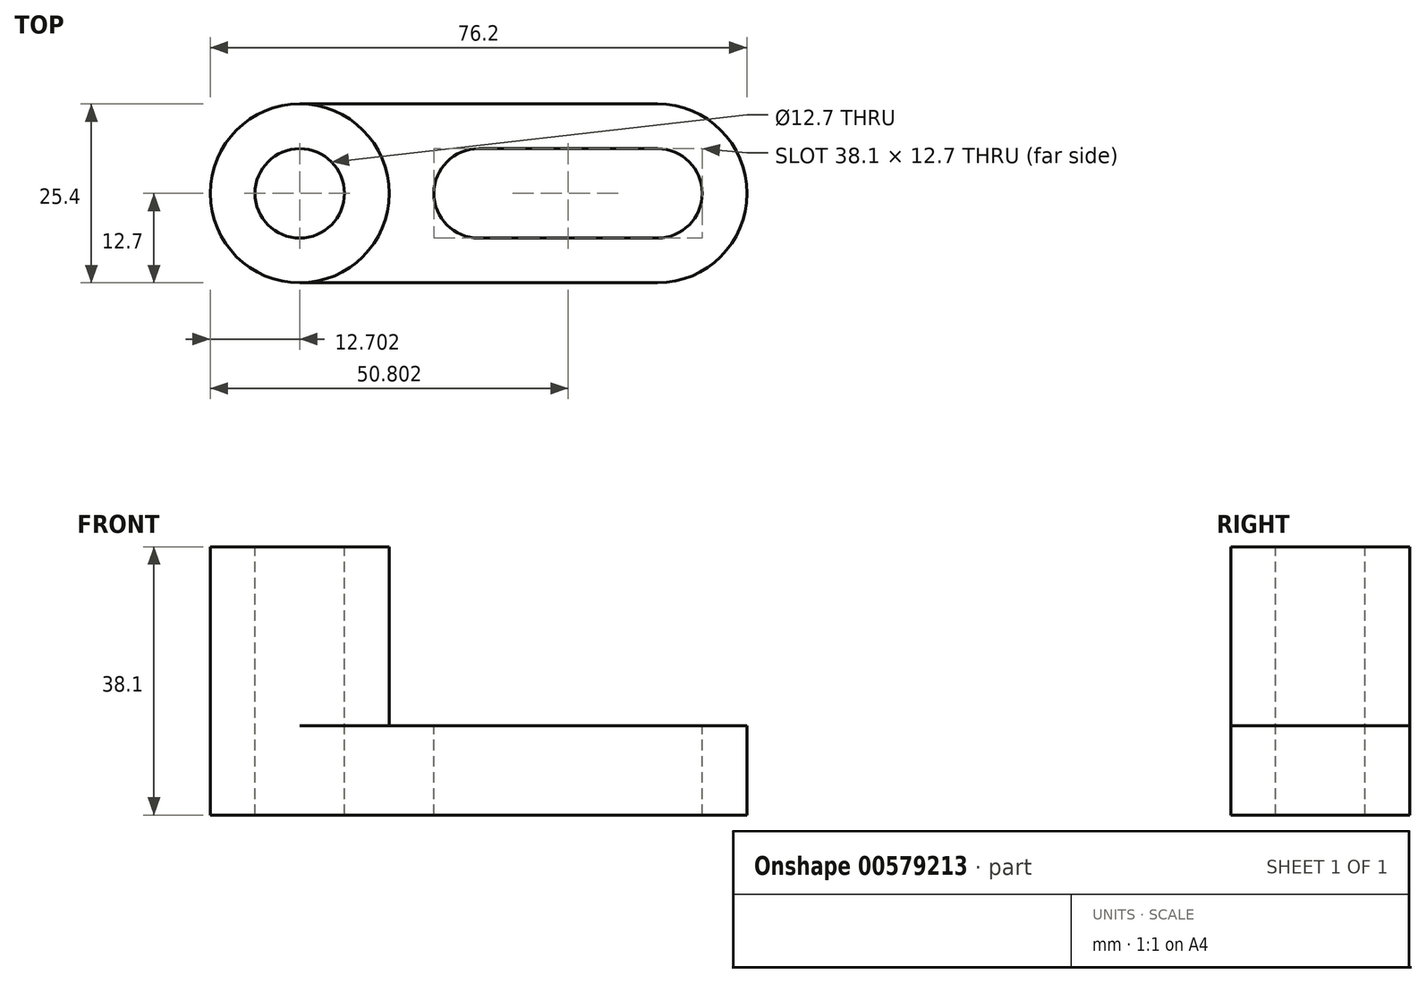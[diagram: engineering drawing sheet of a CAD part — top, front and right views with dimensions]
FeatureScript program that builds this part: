
annotation { "Feature Type Name" : "Feature", "Feature Type Description" : "" }
export const myFeature = defineFeature(function(context is Context, id is Id, definition is map)
    precondition{}
    {
        {
            var Q0;
            Q0=qCreatedBy(makeId("Front.planeOp"),FACE);
            var sketch = newSketch(context, id + "F0", { "sketchPlane" : qUnion([Q0])});
            skLineSegment(sketch, "E0", {"start": v(-84.2, 67.03) * mm, "end": v(-84.2, 28.93) * mm});
            skLineSegment(sketch, "E1", {"start": v(-84.2, 28.93) * mm, "end": v(-8, 28.93) * mm});
            skLineSegment(sketch, "E2", {"start": v(-8, 28.93) * mm, "end": v(-8, 41.63) * mm});
            skLineSegment(sketch, "E3", {"start": v(-8, 41.63) * mm, "end": v(-58.8, 41.63) * mm});
            skLineSegment(sketch, "E4", {"start": v(-58.8, 41.63) * mm, "end": v(-58.8, 67.03) * mm});
            skLineSegment(sketch, "E5", {"start": v(-58.8, 67.03) * mm, "end": v(-84.2, 67.03) * mm});
            skSolve(sketch);
        }
        {
            var Q0;
            Q0=makeQuery(id+"F0.imprint","IMPRINT",FACE,{"disambiguationData":[TD([[makeQuery(id+"F0.imprint","IMPRINT",EDGE,{"derivedFrom":sQuery(id+"F0.wireOp",EDGE,"E0")}),1.0]])]});
            extrude(context, id + "F1", {"entities" : qUnion([Q0]), "depth" : 25.4 * mm, "offsetDistance" : 25.4 * mm});
        }
        {
            var Q0;
            Q0=makeQuery(id+"F1.opExtrude","SWEPT_FACE",FACE,{"disambiguationData":[OSD([sQuery(id+"F0.wireOp",EDGE,"E3")])]});
            var sketch = newSketch(context, id + "F2", { "sketchPlane" : qUnion([Q0])});
            skCircle(sketch, "E6", {"center": v(-46.1, -12.7) * mm, "radius": 6.35 * mm});
            skCircle(sketch, "E7", {"center": v(-20.7, -12.7) * mm, "radius": 6.35 * mm});
            skLineSegment(sketch, "E8", {"start": v(-46.1, -6.35) * mm, "end": v(-20.7, -6.35) * mm});
            skLineSegment(sketch, "E9", {"start": v(-46.1, -19.05) * mm, "end": v(-20.7, -19.05) * mm});
            skSolve(sketch);
        }
        {
            var Q0;
            {var subQ0=sQuery(id+"F2.wireOp",EDGE,"E6");var subQ1=makeQuery(id+"F2.imprint","INTERSECT",VERTEX,{"derivedFrom":[subQ0,sQuery(id+"F2.wireOp",EDGE,"E8")]});Q0=makeQuery(id+"F2.imprint","IMPRINT",FACE,{"disambiguationData":[TD([[makeQuery(id+"F2.imprint","IMPRINT",EDGE,{"disambiguationData":[TD([[subQ1,-1.0]])],"derivedFrom":subQ0}),1.0]])]});}
            var Q1;
            {var subQ0=sQuery(id+"F2.wireOp",EDGE,"E8");Q1=makeQuery(id+"F2.imprint","IMPRINT",FACE,{"disambiguationData":[TD([[makeQuery(id+"F2.imprint","IMPRINT",EDGE,{"derivedFrom":subQ0}),-1.0]])]});}
            var Q2;
            {var subQ0=sQuery(id+"F2.wireOp",EDGE,"E7");var subQ1=makeQuery(id+"F2.imprint","INTERSECT",VERTEX,{"derivedFrom":[subQ0,sQuery(id+"F2.wireOp",EDGE,"E8")]});Q2=makeQuery(id+"F2.imprint","IMPRINT",FACE,{"disambiguationData":[TD([[makeQuery(id+"F2.imprint","IMPRINT",EDGE,{"disambiguationData":[TD([[subQ1,-1.0]])],"derivedFrom":subQ0}),1.0]])]});}
            extrude(context, id + "F3", {"entities" : qUnion([Q0, Q1, Q2]), "operationType" : NewBodyOperationType.REMOVE, "endBound" : BoundingType.THROUGH_ALL, "oppositeDirection" : true, "depth" : 25.4 * mm, "offsetDistance" : 25.4 * mm});
        }
        {
            var Q0;
            Q0=makeQuery(id+"F1.opExtrude","SWEPT_FACE",FACE,{"disambiguationData":[OSD([sQuery(id+"F0.wireOp",EDGE,"E5")])]});
            var sketch = newSketch(context, id + "F4", { "sketchPlane" : qUnion([Q0])});
            skCircle(sketch, "E10", {"center": v(-71.5, -12.7) * mm, "radius": 12.7 * mm});
            skSolve(sketch);
        }
        {
            var Q0;
            {var subQ0=sQuery(id+"F4.wireOp",EDGE,"E10");var subQ1=sQuery(id+"F0.wireOp",EDGE,"E5");var subQ2=makeQuery(id+"F1.opExtrude","CAP_EDGE",EDGE,{"disambiguationData":[OSD([subQ1])],"isStart":true});var subQ3=makeQuery(id+"F4.imprint","INTERSECT",VERTEX,{"derivedFrom":[subQ2,subQ0]});Q0=makeQuery(id+"F4.imprint","IMPRINT",FACE,{"disambiguationData":[TD([[makeQuery(id+"F4.imprint","IMPRINT",EDGE,{"disambiguationData":[TD([[subQ3,1.0]])],"derivedFrom":subQ0}),-1.0]])]});}
            var Q1;
            {var subQ0=sQuery(id+"F4.wireOp",EDGE,"E10");var subQ1=sQuery(id+"F0.wireOp",EDGE,"E5");var subQ4=makeQuery(id+"F1.opExtrude","CAP_EDGE",EDGE,{"disambiguationData":[OSD([subQ1])],"isStart":false});var subQ5=makeQuery(id+"F4.imprint","INTERSECT",VERTEX,{"derivedFrom":[subQ4,subQ0]});Q1=makeQuery(id+"F4.imprint","IMPRINT",FACE,{"disambiguationData":[TD([[makeQuery(id+"F4.imprint","IMPRINT",EDGE,{"disambiguationData":[TD([[subQ5,-1.0]])],"derivedFrom":subQ0}),-1.0]])]});}
            extrude(context, id + "F5", {"entities" : qUnion([Q0, Q1]), "operationType" : NewBodyOperationType.REMOVE, "oppositeDirection" : true, "depth" : 25.4 * mm, "offsetDistance" : 25.4 * mm});
        }
        {
            var Q0;
            Q0=makeQuery(id+"F1.opExtrude","SWEPT_FACE",FACE,{"disambiguationData":[OSD([sQuery(id+"F0.wireOp",EDGE,"E5")])]});
            var sketch = newSketch(context, id + "F6", { "sketchPlane" : qUnion([Q0])});
            skCircle(sketch, "E11", {"center": v(-71.5, -12.7) * mm, "radius": 12.7 * mm});
            skSolve(sketch);
        }
        {
            var Q0;
            {var subQ1=sQuery(id+"F0.wireOp",EDGE,"E5");var subQ2=makeQuery(id+"F1.opExtrude","CAP_EDGE",EDGE,{"disambiguationData":[OSD([subQ1])],"isStart":true});Q0=makeQuery(id+"F6.imprint","IMPRINT",FACE,{"disambiguationData":[TD([[makeQuery(id+"F6.imprint","IMPRINT",EDGE,{"derivedFrom":subQ2}),1.0]])]});}
            var Q1;
            {var subQ1=sQuery(id+"F0.wireOp",EDGE,"E5");var subQ2=makeQuery(id+"F1.opExtrude","CAP_EDGE",EDGE,{"disambiguationData":[OSD([subQ1])],"isStart":false});Q1=makeQuery(id+"F6.imprint","IMPRINT",FACE,{"disambiguationData":[TD([[makeQuery(id+"F6.imprint","IMPRINT",EDGE,{"derivedFrom":subQ2}),-1.0]])]});}
            extrude(context, id + "F7", {"entities" : qUnion([Q0, Q1]), "operationType" : NewBodyOperationType.REMOVE, "endBound" : BoundingType.THROUGH_ALL, "oppositeDirection" : true, "depth" : 25.4 * mm, "offsetDistance" : 25.4 * mm});
        }
        {
            var Q0;
            Q0=makeQuery(id+"F1.opExtrude","SWEPT_FACE",FACE,{"disambiguationData":[OSD([sQuery(id+"F0.wireOp",EDGE,"E5")])]});
            var sketch = newSketch(context, id + "F8", { "sketchPlane" : qUnion([Q0])});
            skCircle(sketch, "E12", {"center": v(-71.5, -12.7) * mm, "radius": 6.35 * mm});
            skSolve(sketch);
        }
        {
            var Q0;
            Q0=makeQuery(id+"F8.imprint","IMPRINT",FACE,{"disambiguationData":[TD([[makeQuery(id+"F8.imprint","IMPRINT",EDGE,{"derivedFrom":sQuery(id+"F8.wireOp",EDGE,"E12")}),1.0]])]});
            extrude(context, id + "F9", {"entities" : qUnion([Q0]), "operationType" : NewBodyOperationType.REMOVE, "endBound" : BoundingType.THROUGH_ALL, "oppositeDirection" : true, "depth" : 25.4 * mm, "offsetDistance" : 25.4 * mm});
        }
        {
            var Q0;
            {var subQ0=sQuery(id+"F0.wireOp",EDGE,"E5");var subQ1=makeQuery(id+"F1.opExtrude","CAP_EDGE",EDGE,{"disambiguationData":[OSD([subQ0])],"isStart":false});var subQ2=sQuery(id+"F0.wireOp",EDGE,"E4");var subQ3=makeQuery(id+"F1.opExtrude","SWEPT_EDGE",EDGE,{"disambiguationData":[OSD([subQ2,subQ0])]});var subQ4=makeQuery(id+"F4.imprint","INTERSECT",VERTEX,{"derivedFrom":[subQ3,subQ1]});var subQ5=sQuery(id+"F4.wireOp",EDGE,"E10");var subQ6=makeQuery(id+"F4.imprint","INTERSECT",VERTEX,{"derivedFrom":[subQ1,subQ5]});var subQ8=makeQuery(id+"F1.opExtrude","CAP_EDGE",EDGE,{"disambiguationData":[OSD([subQ0])],"isStart":true});var subQ9=makeQuery(id+"F4.imprint","INTERSECT",VERTEX,{"derivedFrom":[subQ3,subQ8]});var subQ10=makeQuery(id+"F4.imprint","INTERSECT",VERTEX,{"derivedFrom":[subQ8,subQ5]});Q0=makeQuery(id+"F5.boolean.opBoolean","MERGE",FACE,{"derivedFrom":[makeQuery(id+"F1.opExtrude","SWEPT_FACE",FACE,{"disambiguationData":[OSD([sQuery(id+"F0.wireOp",EDGE,"E3")])]}),makeQuery(id+"F5.opExtrude","CAP_FACE",FACE,{"disambiguationData":[OSD([subQ2,subQ0,subQ5]),TDD([makeQuery(id+"F4.imprint","IMPRINT",EDGE,{"disambiguationData":[TD([[subQ10,1.0]])],"derivedFrom":subQ5}),makeQuery(id+"F4.imprint","IMPRINT",EDGE,{"disambiguationData":[TD([[subQ9,1.0]])],"derivedFrom":subQ3}),makeQuery(id+"F4.imprint","IMPRINT",EDGE,{"disambiguationData":[TD([[subQ10,1.0]])],"derivedFrom":subQ8})])],"isStart":false}),makeQuery(id+"F5.opExtrude","CAP_FACE",FACE,{"disambiguationData":[OSD([subQ2,subQ0,subQ5]),TDD([makeQuery(id+"F4.imprint","IMPRINT",EDGE,{"disambiguationData":[TD([[subQ6,-1.0]])],"derivedFrom":subQ5}),makeQuery(id+"F4.imprint","IMPRINT",EDGE,{"disambiguationData":[TD([[subQ4,-1.0]])],"derivedFrom":subQ3}),makeQuery(id+"F4.imprint","IMPRINT",EDGE,{"disambiguationData":[TD([[subQ6,1.0]])],"derivedFrom":subQ1})])],"isStart":false})]});}
            var sketch = newSketch(context, id + "F10", { "sketchPlane" : qUnion([Q0])});
            skCircle(sketch, "E13", {"center": v(-20.7, -12.7) * mm, "radius": 12.7 * mm});
            skSolve(sketch);
        }
        {
            var Q0;
            {var subQ0=sQuery(id+"F10.wireOp",EDGE,"E13");var subQ3=sQuery(id+"F0.wireOp",EDGE,"E3");var subQ6=makeQuery(id+"F1.opExtrude","SWEPT_EDGE",EDGE,{"disambiguationData":[OSD([sQuery(id+"F0.wireOp",EDGE,"E2"),subQ3])]});var subQ7=makeQuery(id+"F10.imprint","INTERSECT",VERTEX,{"derivedFrom":[subQ6,subQ0]});Q0=makeQuery(id+"F10.imprint","IMPRINT",FACE,{"disambiguationData":[TD([[makeQuery(id+"F10.imprint","IMPRINT",EDGE,{"disambiguationData":[TD([[subQ7,-1.0]])],"derivedFrom":subQ0}),-1.0]])]});}
            var Q1;
            {var subQ0=sQuery(id+"F10.wireOp",EDGE,"E13");var subQ1=sQuery(id+"F0.wireOp",EDGE,"E3");var subQ2=makeQuery(id+"F1.opExtrude","SWEPT_EDGE",EDGE,{"disambiguationData":[OSD([sQuery(id+"F0.wireOp",EDGE,"E2"),subQ1])]});var subQ3=makeQuery(id+"F10.imprint","INTERSECT",VERTEX,{"derivedFrom":[subQ2,subQ0]});Q1=makeQuery(id+"F10.imprint","IMPRINT",FACE,{"disambiguationData":[TD([[makeQuery(id+"F10.imprint","IMPRINT",EDGE,{"disambiguationData":[TD([[subQ3,1.0]])],"derivedFrom":subQ0}),-1.0]])]});}
            extrude(context, id + "F11", {"entities" : qUnion([Q0, Q1]), "operationType" : NewBodyOperationType.REMOVE, "oppositeDirection" : true, "depth" : 25.4 * mm, "offsetDistance" : 25.4 * mm});
        }
    });
